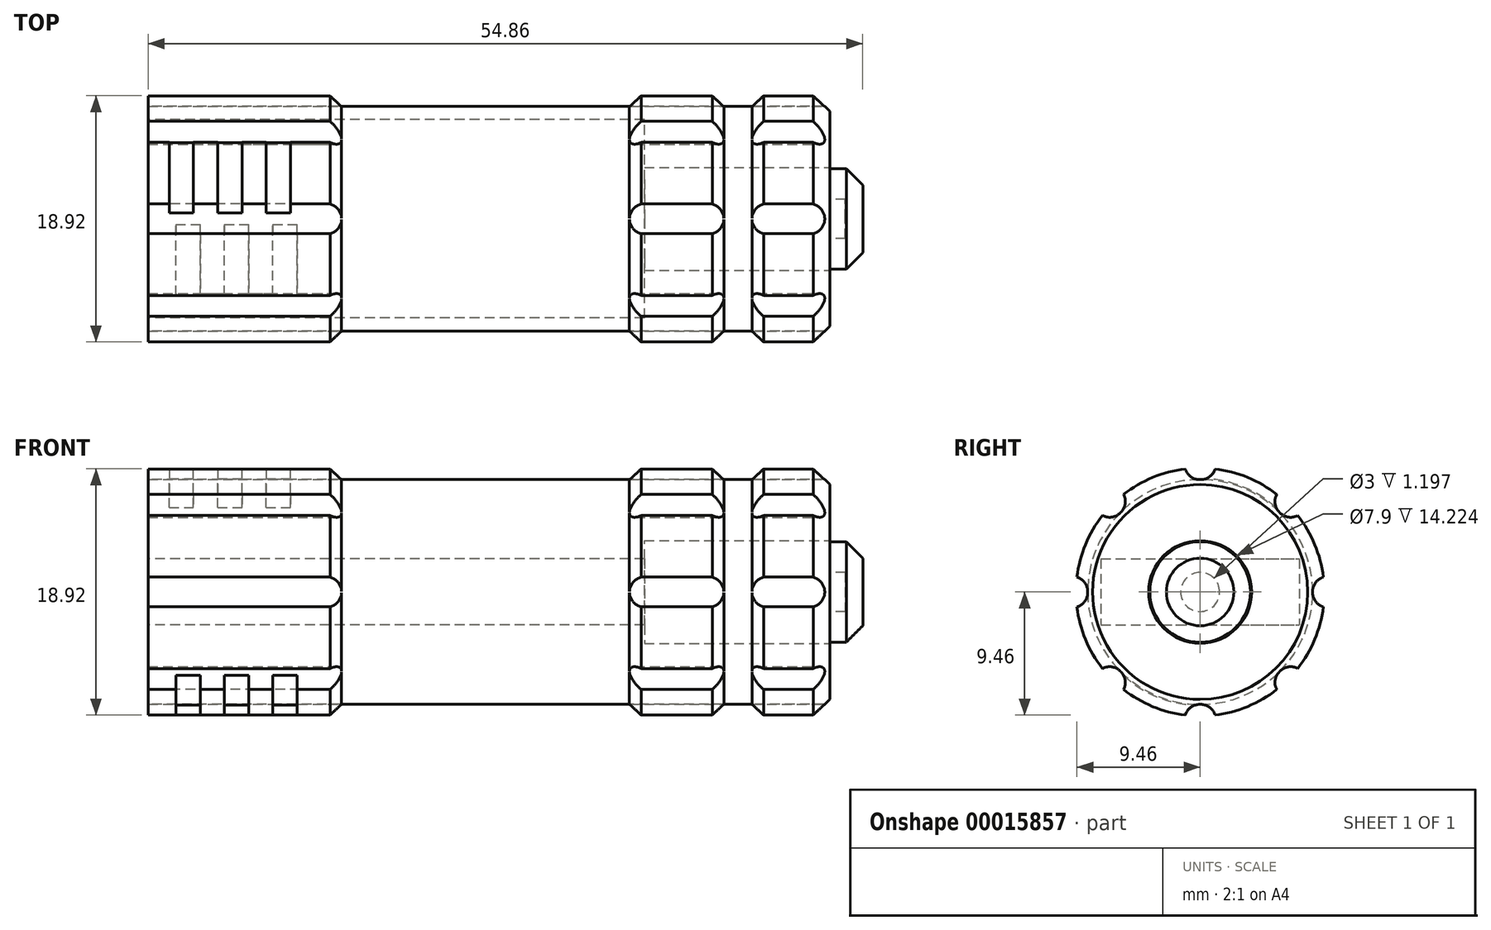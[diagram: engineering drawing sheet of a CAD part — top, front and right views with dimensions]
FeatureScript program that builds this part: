
annotation { "Feature Type Name" : "Feature", "Feature Type Description" : "" }
export const myFeature = defineFeature(function(context is Context, id is Id, definition is map)
    precondition{}
    {
        {
            var Q0;
            Q0=qCreatedBy(makeId("Front.planeOp"),FACE);
            var sketch = newSketch(context, id + "F0", { "sketchPlane" : qUnion([Q0])});
            skLineSegment(sketch, "E0", {"start": v(15.48, 9.52) * mm, "end": v(15.48, 8.64) * mm});
            skLineSegment(sketch, "E1", {"start": v(15.48, 8.64) * mm, "end": v(-2.04, 8.64) * mm});
            skLineSegment(sketch, "E2", {"start": v(-2.04, 8.64) * mm, "end": v(-2.04, 9.52) * mm});
            skLineSegment(sketch, "E3", {"start": v(-2.04, 9.52) * mm, "end": v(-21.1, 9.52) * mm});
            skLineSegment(sketch, "E4", {"start": v(-21.1, 9.52) * mm, "end": v(-21.1, 0) * mm});
            skLineSegment(sketch, "E5", {"start": v(21.83, 9.52) * mm, "end": v(21.83, 8.64) * mm});
            skLineSegment(sketch, "E6", {"start": v(21.83, 8.64) * mm, "end": v(24.88, 8.64) * mm});
            skLineSegment(sketch, "E7", {"start": v(24.88, 8.64) * mm, "end": v(24.88, 9.53) * mm});
            skLineSegment(sketch, "E8", {"start": v(15.48, 9.52) * mm, "end": v(21.83, 9.52) * mm});
            skLineSegment(sketch, "E9", {"start": v(24.88, 9.53) * mm, "end": v(31.23, 9.53) * mm});
            skLineSegment(sketch, "E10", {"start": v(31.23, 9.53) * mm, "end": v(31.23, 3.86) * mm});
            skLineSegment(sketch, "E11", {"start": v(31.23, 3.86) * mm, "end": v(33.77, 3.86) * mm});
            skLineSegment(sketch, "E12", {"start": v(33.77, 3.86) * mm, "end": v(33.77, 0) * mm});
            skLineSegment(sketch, "E13", {"start": v(-21.1, 0) * mm, "end": v(33.77, 0) * mm});
            skLineSegment(sketch, "E14", {"start": v(-2.04, 8.64) * mm, "end": v(-2.04, 0) * mm, "construction": true});
            skSolve(sketch);
        }
        {
            var Q0;
            Q0=qSketchRegion(id+"F0",true);
            var Q1;
            Q1=sQuery(id+"F0.wireOp",EDGE,"E4");
            var Q2;
            Q2=sQuery(id+"F0.wireOp",EDGE,"E3");
            var Q3;
            Q3=sQuery(id+"F0.wireOp",EDGE,"E2");
            var Q4;
            Q4=sQuery(id+"F0.wireOp",EDGE,"E1");
            var Q5;
            Q5=sQuery(id+"F0.wireOp",EDGE,"E0");
            var Q6;
            Q6=sQuery(id+"F0.wireOp",EDGE,"E8");
            var Q7;
            Q7=sQuery(id+"F0.wireOp",EDGE,"E5");
            var Q8;
            Q8=sQuery(id+"F0.wireOp",EDGE,"E6");
            var Q9;
            Q9=sQuery(id+"F0.wireOp",EDGE,"E7");
            var Q10;
            Q10=sQuery(id+"F0.wireOp",EDGE,"E9");
            var Q11;
            Q11=sQuery(id+"F0.wireOp",EDGE,"E10");
            var Q12;
            Q12=sQuery(id+"F0.wireOp",EDGE,"E11");
            var Q13;
            Q13=sQuery(id+"F0.wireOp",EDGE,"E12");
            var Q14;
            Q14=sQuery(id+"F0.wireOp",EDGE,"E13");
            revolve(context, id + "F1", {"entities" : qUnion([Q0]), "surfaceEntities" : qUnion([Q1, Q2, Q3, Q4, Q5, Q6, Q7, Q8, Q9, Q10, Q11, Q12, Q13]), "axis" : qUnion([Q14]), "revolveType" : RevolveType.FULL});
        }
        {
            var Q0;
            Q0=makeQuery(id+"F1.opRevolve","SWEPT_EDGE",EDGE,{"disambiguationData":[OSD([sQuery(id+"F0.wireOp",VERTEX,"E2.end")])]});
            var Q1;
            Q1=makeQuery(id+"F1.opRevolve","SWEPT_EDGE",EDGE,{"disambiguationData":[OSD([sQuery(id+"F0.wireOp",EDGE,"E2"),sQuery(id+"F0.wireOp",EDGE,"E3")])]});
            chamfer(context, id + "F2", {"entities" : qUnion([Q0, Q1]), "width" : 5.08 * mm, "tangentPropagation" : true});
        }
        {
            var Q0;
            Q0=makeQuery(id+"F1.opRevolve","SWEPT_EDGE",EDGE,{"disambiguationData":[OSD([sQuery(id+"F0.wireOp",VERTEX,"E8.start")])]});
            var Q1;
            Q1=makeQuery(id+"F1.opRevolve","SWEPT_EDGE",EDGE,{"disambiguationData":[OSD([sQuery(id+"F0.wireOp",VERTEX,"E5.start")])]});
            var Q2;
            Q2=makeQuery(id+"F1.opRevolve","SWEPT_EDGE",EDGE,{"disambiguationData":[OSD([sQuery(id+"F0.wireOp",VERTEX,"E9.start")])]});
            var Q3;
            Q3=makeQuery(id+"F1.opRevolve","SWEPT_EDGE",EDGE,{"disambiguationData":[OSD([sQuery(id+"F0.wireOp",VERTEX,"E10.start")])]});
            var Q4;
            Q4=makeQuery(id+"F1.opRevolve","SWEPT_EDGE",EDGE,{"disambiguationData":[OSD([sQuery(id+"F0.wireOp",VERTEX,"E12.start")])]});
            var Q5;
            Q5=makeQuery(id+"F1.opRevolve","SWEPT_EDGE",EDGE,{"disambiguationData":[OSD([sQuery(id+"F0.wireOp",EDGE,"E0"),sQuery(id+"F0.wireOp",EDGE,"E8")])]});
            var Q6;
            Q6=makeQuery(id+"F1.opRevolve","SWEPT_EDGE",EDGE,{"disambiguationData":[OSD([sQuery(id+"F0.wireOp",EDGE,"E5"),sQuery(id+"F0.wireOp",EDGE,"E6")])]});
            var Q7;
            Q7=makeQuery(id+"F1.opRevolve","SWEPT_EDGE",EDGE,{"disambiguationData":[OSD([sQuery(id+"F0.wireOp",EDGE,"E7"),sQuery(id+"F0.wireOp",EDGE,"E9")])]});
            var Q8;
            Q8=makeQuery(id+"F1.opRevolve","SWEPT_EDGE",EDGE,{"disambiguationData":[OSD([sQuery(id+"F0.wireOp",EDGE,"E9"),sQuery(id+"F0.wireOp",EDGE,"E10")])]});
            var Q9;
            Q9=makeQuery(id+"F1.opRevolve","SWEPT_EDGE",EDGE,{"disambiguationData":[OSD([sQuery(id+"F0.wireOp",EDGE,"E11"),sQuery(id+"F0.wireOp",EDGE,"E12")])]});
            chamfer(context, id + "F3", {"entities" : qUnion([Q0, Q1, Q2, Q3, Q4, Q5, Q6, Q7, Q8, Q9]), "width" : 1.27 * mm, "tangentPropagation" : true});
        }
        {
            var Q0;
            Q0=makeQuery(id+"F1.opRevolve","SWEPT_FACE",FACE,{"disambiguationData":[OSD([sQuery(id+"F0.wireOp",EDGE,"E4")])]});
            var sketch = newSketch(context, id + "F4", { "sketchPlane" : qUnion([Q0])});
            skLineSegment(sketch, "E15", {"start": v(0, 9.52) * mm, "end": v(0, -9.52) * mm, "construction": true});
            skLineSegment(sketch, "E16", {"start": v(-9.52, 0) * mm, "end": v(9.52, 0) * mm, "construction": true});
            skLineSegment(sketch, "E17", {"start": v(-6.74, -6.74) * mm, "end": v(6.74, 6.74) * mm, "construction": true});
            skLineSegment(sketch, "E18", {"start": v(-6.74, 6.74) * mm, "end": v(6.74, -6.74) * mm, "construction": true});
            skLineSegment(sketch, "E19", {"start": v(-5.88, 7.5) * mm, "end": v(0, 0) * mm});
            skLineSegment(sketch, "E20", {"start": v(0, 0) * mm, "end": v(-7.5, 5.88) * mm});
            skLineSegment(sketch, "E21", {"start": v(-5.88, 7.5) * mm, "end": v(-6.74, 6.74) * mm, "construction": true});
            skLineSegment(sketch, "E22", {"start": v(-7.5, 5.88) * mm, "end": v(-6.74, 6.74) * mm, "construction": true});
            skLineSegment(sketch, "E23", {"start": v(-1.14, 9.46) * mm, "end": v(0, 0) * mm});
            skLineSegment(sketch, "E24", {"start": v(0, 0) * mm, "end": v(1.14, 9.46) * mm});
            skLineSegment(sketch, "E25", {"start": v(1.14, 9.46) * mm, "end": v(0, 9.52) * mm, "construction": true});
            skLineSegment(sketch, "E26", {"start": v(-1.14, 9.46) * mm, "end": v(0, 9.52) * mm, "construction": true});
            skLineSegment(sketch, "E27", {"start": v(0, 0) * mm, "end": v(5.88, 7.5) * mm});
            skLineSegment(sketch, "E28", {"start": v(5.88, 7.5) * mm, "end": v(6.74, 6.74) * mm, "construction": true});
            skLineSegment(sketch, "E29", {"start": v(6.74, 6.74) * mm, "end": v(7.5, 5.88) * mm, "construction": true});
            skLineSegment(sketch, "E30", {"start": v(7.5, 5.88) * mm, "end": v(0, 0) * mm});
            skLineSegment(sketch, "E31", {"start": v(0, 0) * mm, "end": v(9.46, 1.14) * mm});
            skLineSegment(sketch, "E32", {"start": v(9.46, 1.14) * mm, "end": v(9.53, 0) * mm, "construction": true});
            skLineSegment(sketch, "E33", {"start": v(0, 0) * mm, "end": v(9.46, -1.14) * mm});
            skLineSegment(sketch, "E34", {"start": v(9.46, -1.14) * mm, "end": v(9.53, 0) * mm, "construction": true});
            skLineSegment(sketch, "E35", {"start": v(0, 0) * mm, "end": v(7.5, -5.88) * mm});
            skLineSegment(sketch, "E36", {"start": v(7.5, -5.88) * mm, "end": v(6.74, -6.74) * mm, "construction": true});
            skLineSegment(sketch, "E37", {"start": v(0, 0) * mm, "end": v(5.88, -7.5) * mm});
            skLineSegment(sketch, "E38", {"start": v(5.88, -7.5) * mm, "end": v(6.74, -6.74) * mm, "construction": true});
            skLineSegment(sketch, "E39", {"start": v(0, 0) * mm, "end": v(1.14, -9.46) * mm});
            skLineSegment(sketch, "E40", {"start": v(1.14, -9.46) * mm, "end": v(0, -9.52) * mm, "construction": true});
            skLineSegment(sketch, "E41", {"start": v(0, 0) * mm, "end": v(-1.14, -9.46) * mm});
            skLineSegment(sketch, "E42", {"start": v(-1.14, -9.46) * mm, "end": v(0, -9.52) * mm, "construction": true});
            skLineSegment(sketch, "E43", {"start": v(0, 0) * mm, "end": v(-5.88, -7.5) * mm});
            skLineSegment(sketch, "E44", {"start": v(-5.88, -7.5) * mm, "end": v(-6.74, -6.74) * mm, "construction": true});
            skLineSegment(sketch, "E45", {"start": v(0, 0) * mm, "end": v(-7.5, -5.88) * mm});
            skLineSegment(sketch, "E46", {"start": v(-7.5, -5.88) * mm, "end": v(-6.74, -6.74) * mm, "construction": true});
            skLineSegment(sketch, "E47", {"start": v(0, 0) * mm, "end": v(-9.46, -1.14) * mm});
            skLineSegment(sketch, "E48", {"start": v(-9.46, -1.14) * mm, "end": v(-9.52, 0) * mm, "construction": true});
            skLineSegment(sketch, "E49", {"start": v(0, 0) * mm, "end": v(-9.46, 1.14) * mm});
            skLineSegment(sketch, "E50", {"start": v(-9.46, 1.14) * mm, "end": v(-9.52, 0) * mm, "construction": true});
            skLineSegment(sketch, "E51", {"start": v(-5.88, 7.5) * mm, "end": v(-1.14, 9.46) * mm, "construction": true});
            skLineSegment(sketch, "E52", {"start": v(1.14, 9.46) * mm, "end": v(5.88, 7.5) * mm, "construction": true});
            skLineSegment(sketch, "E53", {"start": v(7.5, 5.88) * mm, "end": v(9.46, 1.14) * mm, "construction": true});
            skLineSegment(sketch, "E54", {"start": v(9.46, -1.14) * mm, "end": v(7.5, -5.88) * mm, "construction": true});
            skLineSegment(sketch, "E55", {"start": v(5.88, -7.5) * mm, "end": v(1.14, -9.46) * mm, "construction": true});
            skLineSegment(sketch, "E56", {"start": v(-1.14, -9.46) * mm, "end": v(-5.88, -7.5) * mm, "construction": true});
            skLineSegment(sketch, "E57", {"start": v(-7.5, -5.88) * mm, "end": v(-9.46, -1.14) * mm, "construction": true});
            skLineSegment(sketch, "E58", {"start": v(-9.46, 1.14) * mm, "end": v(-7.5, 5.88) * mm, "construction": true});
            skCircle(sketch, "E59", {"center": v(0, 0) * mm, "radius": 8.64 * mm});
            skLineSegment(sketch, "E60", {"start": v(0, 9.52) * mm, "end": v(0, 8.64) * mm, "construction": true});
            skSolve(sketch);
        }
        {
            var Q0;
            {var subQ3=sQuery(id+"F4.wireOp",EDGE,"E23");var subQ5=sQuery(id+"F4.wireOp",EDGE,"E59");var subQ7=makeQuery(id+"F4.imprint","INTERSECT",VERTEX,{"derivedFrom":[subQ3,subQ5]});Q0=makeQuery(id+"F4.imprint","IMPRINT",FACE,{"disambiguationData":[TD([[makeQuery(id+"F4.imprint","IMPRINT",EDGE,{"disambiguationData":[TD([[subQ7,1.0]])],"derivedFrom":subQ5}),-1.0]])]});}
            var Q1;
            {var subQ3=sQuery(id+"F4.wireOp",EDGE,"E19");var subQ5=sQuery(id+"F4.wireOp",EDGE,"E59");var subQ7=makeQuery(id+"F4.imprint","INTERSECT",VERTEX,{"derivedFrom":[subQ3,subQ5]});Q1=makeQuery(id+"F4.imprint","IMPRINT",FACE,{"disambiguationData":[TD([[makeQuery(id+"F4.imprint","IMPRINT",EDGE,{"disambiguationData":[TD([[subQ7,-1.0]])],"derivedFrom":subQ5}),-1.0]])]});}
            var Q2;
            {var subQ3=sQuery(id+"F4.wireOp",EDGE,"E47");var subQ5=sQuery(id+"F4.wireOp",EDGE,"E59");var subQ7=makeQuery(id+"F4.imprint","INTERSECT",VERTEX,{"derivedFrom":[subQ3,subQ5]});Q2=makeQuery(id+"F4.imprint","IMPRINT",FACE,{"disambiguationData":[TD([[makeQuery(id+"F4.imprint","IMPRINT",EDGE,{"disambiguationData":[TD([[subQ7,1.0]])],"derivedFrom":subQ5}),-1.0]])]});}
            var Q3;
            {var subQ3=sQuery(id+"F4.wireOp",EDGE,"E43");var subQ5=sQuery(id+"F4.wireOp",EDGE,"E59");var subQ7=makeQuery(id+"F4.imprint","INTERSECT",VERTEX,{"derivedFrom":[subQ3,subQ5]});Q3=makeQuery(id+"F4.imprint","IMPRINT",FACE,{"disambiguationData":[TD([[makeQuery(id+"F4.imprint","IMPRINT",EDGE,{"disambiguationData":[TD([[subQ7,1.0]])],"derivedFrom":subQ5}),-1.0]])]});}
            var Q4;
            {var subQ3=sQuery(id+"F4.wireOp",EDGE,"E39");var subQ5=sQuery(id+"F4.wireOp",EDGE,"E59");var subQ7=makeQuery(id+"F4.imprint","INTERSECT",VERTEX,{"derivedFrom":[subQ3,subQ5]});Q4=makeQuery(id+"F4.imprint","IMPRINT",FACE,{"disambiguationData":[TD([[makeQuery(id+"F4.imprint","IMPRINT",EDGE,{"disambiguationData":[TD([[subQ7,1.0]])],"derivedFrom":subQ5}),-1.0]])]});}
            var Q5;
            {var subQ3=sQuery(id+"F4.wireOp",EDGE,"E35");var subQ5=sQuery(id+"F4.wireOp",EDGE,"E59");var subQ7=makeQuery(id+"F4.imprint","INTERSECT",VERTEX,{"derivedFrom":[subQ3,subQ5]});Q5=makeQuery(id+"F4.imprint","IMPRINT",FACE,{"disambiguationData":[TD([[makeQuery(id+"F4.imprint","IMPRINT",EDGE,{"disambiguationData":[TD([[subQ7,1.0]])],"derivedFrom":subQ5}),-1.0]])]});}
            var Q6;
            {var subQ3=sQuery(id+"F4.wireOp",EDGE,"E31");var subQ5=sQuery(id+"F4.wireOp",EDGE,"E59");var subQ7=makeQuery(id+"F4.imprint","INTERSECT",VERTEX,{"derivedFrom":[subQ3,subQ5]});Q6=makeQuery(id+"F4.imprint","IMPRINT",FACE,{"disambiguationData":[TD([[makeQuery(id+"F4.imprint","IMPRINT",EDGE,{"disambiguationData":[TD([[subQ7,1.0]])],"derivedFrom":subQ5}),-1.0]])]});}
            var Q7;
            {var subQ3=sQuery(id+"F4.wireOp",EDGE,"E27");var subQ5=sQuery(id+"F4.wireOp",EDGE,"E59");var subQ7=makeQuery(id+"F4.imprint","INTERSECT",VERTEX,{"derivedFrom":[subQ3,subQ5]});Q7=makeQuery(id+"F4.imprint","IMPRINT",FACE,{"disambiguationData":[TD([[makeQuery(id+"F4.imprint","IMPRINT",EDGE,{"disambiguationData":[TD([[subQ7,1.0]])],"derivedFrom":subQ5}),-1.0]])]});}
            var Q8;
            Q8=makeQuery(id+"F1.opRevolve","SWEPT_FACE",FACE,{"disambiguationData":[OSD([sQuery(id+"F0.wireOp",EDGE,"E10")])]});
            extrude(context, id + "F5", {"entities" : qUnion([Q0, Q1, Q2, Q3, Q4, Q5, Q6, Q7]), "operationType" : NewBodyOperationType.REMOVE, "endBound" : BoundingType.THROUGH_ALL, "oppositeDirection" : true, "endBoundEntityFace" : qUnion([Q8]), "depth" : 25.4 * mm});
        }
        {
            var Q0;
            Q0=qCreatedBy(makeId("Front.planeOp"),FACE);
            var sketch = newSketch(context, id + "F6", { "sketchPlane" : qUnion([Q0])});
            skLineSegment(sketch, "E61", {"start": v(-21.13, 9.56) * mm, "end": v(-19.47, 9.56) * mm, "construction": true});
            skLineSegment(sketch, "E62", {"start": v(-19.47, 9.56) * mm, "end": v(-19.47, 8.72) * mm});
            skLineSegment(sketch, "E63", {"start": v(-19.47, 8.72) * mm, "end": v(-17.6, 8.72) * mm});
            skLineSegment(sketch, "E64", {"start": v(-17.6, 8.72) * mm, "end": v(-17.6, 9.56) * mm});
            skLineSegment(sketch, "E65", {"start": v(-17.6, 9.56) * mm, "end": v(-15.75, 9.56) * mm, "construction": true});
            skLineSegment(sketch, "E66", {"start": v(-15.75, 9.56) * mm, "end": v(-15.75, 8.72) * mm});
            skLineSegment(sketch, "E67", {"start": v(-15.75, 8.72) * mm, "end": v(-13.88, 8.72) * mm});
            skLineSegment(sketch, "E68", {"start": v(-13.88, 8.72) * mm, "end": v(-13.88, 9.56) * mm});
            skLineSegment(sketch, "E69", {"start": v(-13.88, 9.56) * mm, "end": v(-12.03, 9.56) * mm, "construction": true});
            skLineSegment(sketch, "E70", {"start": v(-12.03, 9.56) * mm, "end": v(-12.03, 8.72) * mm});
            skLineSegment(sketch, "E71", {"start": v(-12.03, 8.72) * mm, "end": v(-10.16, 8.72) * mm});
            skLineSegment(sketch, "E72", {"start": v(-10.16, 8.72) * mm, "end": v(-10.16, 9.56) * mm});
            skLineSegment(sketch, "E73", {"start": v(-10.16, 9.56) * mm, "end": v(-7.16, 9.56) * mm, "construction": true});
            skLineSegment(sketch, "E74", {"start": v(-21.13, 0) * mm, "end": v(-7.1, 0) * mm, "construction": true});
            skLineSegment(sketch, "E75", {"start": v(-21.13, 9.56) * mm, "end": v(-21.13, 0) * mm, "construction": true});
            skLineSegment(sketch, "E76", {"start": v(-19.47, 9.56) * mm, "end": v(-17.6, 9.56) * mm});
            skLineSegment(sketch, "E77", {"start": v(-15.75, 9.56) * mm, "end": v(-13.88, 9.56) * mm});
            skLineSegment(sketch, "E78", {"start": v(-12.03, 9.56) * mm, "end": v(-10.16, 9.56) * mm});
            skSolve(sketch);
        }
        {
            var Q0;
            Q0=qSketchRegion(id+"F6",true);
            var Q1;
            Q1=sQuery(id+"F6.wireOp",EDGE,"E74");
            revolve(context, id + "F7", {"operationType" : NewBodyOperationType.REMOVE, "entities" : qUnion([Q0]), "axis" : qUnion([Q1]), "revolveType" : RevolveType.ONE_DIRECTION, "oppositeDirection" : true, "angle" : 41.96 * degree});
        }
        {
            var Q0;
            Q0=qCreatedBy(makeId("Front.planeOp"),FACE);
            var sketch = newSketch(context, id + "F8", { "sketchPlane" : qUnion([Q0])});
            skLineSegment(sketch, "E79", {"start": v(-21.02, -8.7) * mm, "end": v(-18.96, -8.7) * mm, "construction": true});
            skLineSegment(sketch, "E80", {"start": v(-18.96, -8.7) * mm, "end": v(-18.96, -9.55) * mm});
            skLineSegment(sketch, "E81", {"start": v(-18.96, -9.55) * mm, "end": v(-17.08, -9.55) * mm});
            skLineSegment(sketch, "E82", {"start": v(-17.08, -9.55) * mm, "end": v(-17.08, -8.7) * mm});
            skLineSegment(sketch, "E83", {"start": v(-17.08, -8.7) * mm, "end": v(-15.24, -8.7) * mm, "construction": true});
            skLineSegment(sketch, "E84", {"start": v(-15.24, -8.7) * mm, "end": v(-15.24, -9.55) * mm});
            skLineSegment(sketch, "E85", {"start": v(-15.24, -9.55) * mm, "end": v(-13.36, -9.55) * mm});
            skLineSegment(sketch, "E86", {"start": v(-13.36, -9.55) * mm, "end": v(-13.36, -8.7) * mm});
            skLineSegment(sketch, "E87", {"start": v(-13.36, -8.7) * mm, "end": v(-11.52, -8.7) * mm, "construction": true});
            skLineSegment(sketch, "E88", {"start": v(-11.52, -8.7) * mm, "end": v(-11.52, -9.55) * mm});
            skLineSegment(sketch, "E89", {"start": v(-11.52, -9.55) * mm, "end": v(-9.65, -9.55) * mm});
            skLineSegment(sketch, "E90", {"start": v(-9.65, -9.55) * mm, "end": v(-9.65, -8.7) * mm});
            skLineSegment(sketch, "E91", {"start": v(-46.06, -8.7) * mm, "end": v(-9.65, -8.7) * mm, "construction": true});
            skLineSegment(sketch, "E92", {"start": v(-46.06, -0.05) * mm, "end": v(-21.02, -0.05) * mm, "construction": true});
            skLineSegment(sketch, "E93", {"start": v(-21.02, -0.05) * mm, "end": v(-21.02, -8.7) * mm, "construction": true});
            skLineSegment(sketch, "E94", {"start": v(-18.96, -8.7) * mm, "end": v(-17.08, -8.7) * mm});
            skLineSegment(sketch, "E95", {"start": v(-15.24, -8.7) * mm, "end": v(-13.36, -8.7) * mm});
            skLineSegment(sketch, "E96", {"start": v(-11.52, -8.7) * mm, "end": v(-9.65, -8.7) * mm});
            skLineSegment(sketch, "E97", {"start": v(-46.06, -0.05) * mm, "end": v(-46.06, -8.7) * mm, "construction": true});
            skSolve(sketch);
        }
        {
            var Q0;
            Q0=makeQuery(id+"F8.imprint","IMPRINT",FACE,{"disambiguationData":[TD([[makeQuery(id+"F8.imprint","IMPRINT",EDGE,{"derivedFrom":sQuery(id+"F8.wireOp",EDGE,"E88")}),1.0]])]});
            var Q1;
            Q1=makeQuery(id+"F8.imprint","IMPRINT",FACE,{"disambiguationData":[TD([[makeQuery(id+"F8.imprint","IMPRINT",EDGE,{"derivedFrom":sQuery(id+"F8.wireOp",EDGE,"E80")}),1.0]])]});
            var Q2;
            Q2=makeQuery(id+"F8.imprint","IMPRINT",FACE,{"disambiguationData":[TD([[makeQuery(id+"F8.imprint","IMPRINT",EDGE,{"derivedFrom":sQuery(id+"F8.wireOp",EDGE,"E84")}),1.0]])]});
            var Q3;
            Q3=sQuery(id+"F8.wireOp",EDGE,"E95");
            var Q4;
            Q4=sQuery(id+"F8.wireOp",EDGE,"E89");
            var Q5;
            Q5=sQuery(id+"F8.wireOp",EDGE,"E85");
            var Q6;
            Q6=sQuery(id+"F8.wireOp",EDGE,"E81");
            var Q7;
            Q7=sQuery(id+"F8.wireOp",EDGE,"E96");
            var Q8;
            Q8=sQuery(id+"F8.wireOp",EDGE,"E94");
            var Q9;
            Q9=sQuery(id+"F8.wireOp",EDGE,"E90");
            var Q10;
            Q10=sQuery(id+"F8.wireOp",EDGE,"E86");
            var Q11;
            Q11=sQuery(id+"F8.wireOp",EDGE,"E82");
            var Q12;
            Q12=sQuery(id+"F8.wireOp",EDGE,"E88");
            var Q13;
            Q13=sQuery(id+"F8.wireOp",EDGE,"E84");
            var Q14;
            Q14=sQuery(id+"F8.wireOp",EDGE,"E80");
            var Q15;
            Q15=sQuery(id+"F8.wireOp",EDGE,"E92");
            revolve(context, id + "F9", {"operationType" : NewBodyOperationType.REMOVE, "entities" : qUnion([Q0, Q1, Q2]), "surfaceEntities" : qUnion([Q3, Q4, Q5, Q6, Q7, Q8, Q9, Q10, Q11, Q12, Q13, Q14]), "axis" : qUnion([Q15]), "revolveType" : RevolveType.ONE_DIRECTION, "oppositeDirection" : true, "angle" : 41.45 * degree});
        }
        {
            var Q0;
            Q0=makeQuery(id+"F1.opRevolve","SWEPT_FACE",FACE,{"disambiguationData":[OSD([sQuery(id+"F0.wireOp",EDGE,"E4")])]});
            var sketch = newSketch(context, id + "F10", { "sketchPlane" : qUnion([Q0])});
            skLineSegment(sketch, "E98.rect.bottom", {"start": v(7.62, 2.54) * mm, "end": v(-7.62, 2.54) * mm});
            skLineSegment(sketch, "E98.rect.top", {"start": v(7.62, -2.54) * mm, "end": v(-7.62, -2.54) * mm});
            skLineSegment(sketch, "E98.rect.left", {"start": v(7.62, 2.54) * mm, "end": v(7.62, -2.54) * mm});
            skLineSegment(sketch, "E98.rect.right", {"start": v(-7.62, 2.54) * mm, "end": v(-7.62, -2.54) * mm});
            skPoint(sketch, "E98.rect.middle", {"position": v(0, 0) * mm});
            skSolve(sketch);
        }
        {
            var Q0;
            Q0 = qSketchRegion(id + "F10", true);
            extrude(context, id + "F11", {"entities" : qUnion([Q0]), "operationType" : NewBodyOperationType.REMOVE, "oppositeDirection" : true, "depth" : 38.1 * mm});
        }
        {
            var Q0;
            Q0=makeQuery(id+"F1.opRevolve","SWEPT_FACE",FACE,{"disambiguationData":[OSD([sQuery(id+"F0.wireOp",EDGE,"E10")])]});
            var sketch = newSketch(context, id + "F12", { "sketchPlane" : qUnion([Q0])});
            skCircle(sketch, "E99", {"center": v(0, 0) * mm, "radius": 3.95 * mm});
            skSolve(sketch);
        }
        {
            var Q0;
            Q0 = qSketchRegion(id + "F12", true);
            var Q1;
            Q1=makeQuery(id+"F11.boolean.opBoolean","COPY",FACE,{"derivedFrom":makeQuery(id+"F11.opExtrude","CAP_FACE",FACE,{"disambiguationData":[OSD([sQuery(id+"F10.wireOp",EDGE,"E98.rect.bottom"),sQuery(id+"F10.wireOp",EDGE,"E98.rect.top"),sQuery(id+"F10.wireOp",EDGE,"E98.rect.left"),sQuery(id+"F10.wireOp",EDGE,"E98.rect.right")])],"isStart":false})});
            extrude(context, id + "F13", {"entities" : qUnion([Q0]), "operationType" : NewBodyOperationType.REMOVE, "endBound" : BoundingType.UP_TO_SURFACE, "oppositeDirection" : true, "endBoundEntityFace" : qUnion([Q1]), "depth" : 25.4 * mm});
        }
        {
            var Q0;
            Q0=makeQuery(id+"F5.boolean.opBoolean","COPY",EDGE,{"disambiguationData":[OD(0.0)],"derivedFrom":makeQuery(id+"F5.opExtrude","SWEPT_EDGE",EDGE,{"disambiguationData":[OSD([sQuery(id+"F4.wireOp",EDGE,"E47"),sQuery(id+"F4.wireOp",EDGE,"E59")])]})});
            var Q1;
            Q1=makeQuery(id+"F5.boolean.opBoolean","COPY",EDGE,{"disambiguationData":[OD(0.0)],"derivedFrom":makeQuery(id+"F5.opExtrude","SWEPT_EDGE",EDGE,{"disambiguationData":[OSD([sQuery(id+"F4.wireOp",EDGE,"E49"),sQuery(id+"F4.wireOp",EDGE,"E59")])]})});
            var Q2;
            Q2=makeQuery(id+"F5.boolean.opBoolean","COPY",EDGE,{"disambiguationData":[OD(2.0)],"derivedFrom":makeQuery(id+"F5.opExtrude","SWEPT_EDGE",EDGE,{"disambiguationData":[OSD([sQuery(id+"F4.wireOp",EDGE,"E47"),sQuery(id+"F4.wireOp",EDGE,"E59")])]})});
            var Q3;
            Q3=makeQuery(id+"F5.boolean.opBoolean","COPY",EDGE,{"disambiguationData":[OD(1.0)],"derivedFrom":makeQuery(id+"F5.opExtrude","SWEPT_EDGE",EDGE,{"disambiguationData":[OSD([sQuery(id+"F4.wireOp",EDGE,"E47"),sQuery(id+"F4.wireOp",EDGE,"E59")])]})});
            var Q4;
            Q4=makeQuery(id+"F5.boolean.opBoolean","COPY",EDGE,{"disambiguationData":[OD(2.0)],"derivedFrom":makeQuery(id+"F5.opExtrude","SWEPT_EDGE",EDGE,{"disambiguationData":[OSD([sQuery(id+"F4.wireOp",EDGE,"E43"),sQuery(id+"F4.wireOp",EDGE,"E59")])]})});
            var Q5;
            Q5=makeQuery(id+"F5.boolean.opBoolean","COPY",EDGE,{"disambiguationData":[OD(1.0)],"derivedFrom":makeQuery(id+"F5.opExtrude","SWEPT_EDGE",EDGE,{"disambiguationData":[OSD([sQuery(id+"F4.wireOp",EDGE,"E43"),sQuery(id+"F4.wireOp",EDGE,"E59")])]})});
            var Q6;
            Q6=makeQuery(id+"F5.boolean.opBoolean","COPY",EDGE,{"disambiguationData":[OD(0.0)],"derivedFrom":makeQuery(id+"F5.opExtrude","SWEPT_EDGE",EDGE,{"disambiguationData":[OSD([sQuery(id+"F4.wireOp",EDGE,"E43"),sQuery(id+"F4.wireOp",EDGE,"E59")])]})});
            var Q7;
            Q7=makeQuery(id+"F5.boolean.opBoolean","COPY",EDGE,{"disambiguationData":[OD(0.0)],"derivedFrom":makeQuery(id+"F5.opExtrude","SWEPT_EDGE",EDGE,{"disambiguationData":[OSD([sQuery(id+"F4.wireOp",EDGE,"E39"),sQuery(id+"F4.wireOp",EDGE,"E59")])]})});
            var Q8;
            Q8=makeQuery(id+"F5.boolean.opBoolean","COPY",EDGE,{"disambiguationData":[OD(2.0)],"derivedFrom":makeQuery(id+"F5.opExtrude","SWEPT_EDGE",EDGE,{"disambiguationData":[OSD([sQuery(id+"F4.wireOp",EDGE,"E39"),sQuery(id+"F4.wireOp",EDGE,"E59")])]})});
            var Q9;
            Q9=makeQuery(id+"F5.boolean.opBoolean","COPY",EDGE,{"disambiguationData":[OD(1.0)],"derivedFrom":makeQuery(id+"F5.opExtrude","SWEPT_EDGE",EDGE,{"disambiguationData":[OSD([sQuery(id+"F4.wireOp",EDGE,"E39"),sQuery(id+"F4.wireOp",EDGE,"E59")])]})});
            var Q10;
            Q10=makeQuery(id+"F5.boolean.opBoolean","COPY",EDGE,{"disambiguationData":[OD(1.0)],"derivedFrom":makeQuery(id+"F5.opExtrude","SWEPT_EDGE",EDGE,{"disambiguationData":[OSD([sQuery(id+"F4.wireOp",EDGE,"E35"),sQuery(id+"F4.wireOp",EDGE,"E59")])]})});
            var Q11;
            Q11=makeQuery(id+"F5.boolean.opBoolean","COPY",EDGE,{"disambiguationData":[OD(2.0)],"derivedFrom":makeQuery(id+"F5.opExtrude","SWEPT_EDGE",EDGE,{"disambiguationData":[OSD([sQuery(id+"F4.wireOp",EDGE,"E35"),sQuery(id+"F4.wireOp",EDGE,"E59")])]})});
            var Q12;
            Q12=makeQuery(id+"F5.boolean.opBoolean","COPY",EDGE,{"disambiguationData":[OD(0.0)],"derivedFrom":makeQuery(id+"F5.opExtrude","SWEPT_EDGE",EDGE,{"disambiguationData":[OSD([sQuery(id+"F4.wireOp",EDGE,"E35"),sQuery(id+"F4.wireOp",EDGE,"E59")])]})});
            var Q13;
            Q13=makeQuery(id+"F5.boolean.opBoolean","COPY",EDGE,{"disambiguationData":[OD(0.0)],"derivedFrom":makeQuery(id+"F5.opExtrude","SWEPT_EDGE",EDGE,{"disambiguationData":[OSD([sQuery(id+"F4.wireOp",EDGE,"E31"),sQuery(id+"F4.wireOp",EDGE,"E59")])]})});
            var Q14;
            Q14=makeQuery(id+"F5.boolean.opBoolean","COPY",EDGE,{"disambiguationData":[OD(2.0)],"derivedFrom":makeQuery(id+"F5.opExtrude","SWEPT_EDGE",EDGE,{"disambiguationData":[OSD([sQuery(id+"F4.wireOp",EDGE,"E31"),sQuery(id+"F4.wireOp",EDGE,"E59")])]})});
            var Q15;
            Q15=makeQuery(id+"F5.boolean.opBoolean","COPY",EDGE,{"disambiguationData":[OD(1.0)],"derivedFrom":makeQuery(id+"F5.opExtrude","SWEPT_EDGE",EDGE,{"disambiguationData":[OSD([sQuery(id+"F4.wireOp",EDGE,"E31"),sQuery(id+"F4.wireOp",EDGE,"E59")])]})});
            var Q16;
            Q16=makeQuery(id+"F5.boolean.opBoolean","COPY",EDGE,{"disambiguationData":[OD(0.0)],"derivedFrom":makeQuery(id+"F5.opExtrude","SWEPT_EDGE",EDGE,{"disambiguationData":[OSD([sQuery(id+"F4.wireOp",EDGE,"E27"),sQuery(id+"F4.wireOp",EDGE,"E59")])]})});
            var Q17;
            Q17=makeQuery(id+"F5.boolean.opBoolean","COPY",EDGE,{"disambiguationData":[OD(2.0)],"derivedFrom":makeQuery(id+"F5.opExtrude","SWEPT_EDGE",EDGE,{"disambiguationData":[OSD([sQuery(id+"F4.wireOp",EDGE,"E27"),sQuery(id+"F4.wireOp",EDGE,"E59")])]})});
            var Q18;
            Q18=makeQuery(id+"F5.boolean.opBoolean","COPY",EDGE,{"disambiguationData":[OD(1.0)],"derivedFrom":makeQuery(id+"F5.opExtrude","SWEPT_EDGE",EDGE,{"disambiguationData":[OSD([sQuery(id+"F4.wireOp",EDGE,"E27"),sQuery(id+"F4.wireOp",EDGE,"E59")])]})});
            var Q19;
            Q19=makeQuery(id+"F5.boolean.opBoolean","COPY",EDGE,{"disambiguationData":[OD(0.0)],"derivedFrom":makeQuery(id+"F5.opExtrude","SWEPT_EDGE",EDGE,{"disambiguationData":[OSD([sQuery(id+"F4.wireOp",EDGE,"E23"),sQuery(id+"F4.wireOp",EDGE,"E59")])]})});
            var Q20;
            Q20=makeQuery(id+"F5.boolean.opBoolean","COPY",EDGE,{"disambiguationData":[OD(2.0)],"derivedFrom":makeQuery(id+"F5.opExtrude","SWEPT_EDGE",EDGE,{"disambiguationData":[OSD([sQuery(id+"F4.wireOp",EDGE,"E23"),sQuery(id+"F4.wireOp",EDGE,"E59")])]})});
            var Q21;
            Q21=makeQuery(id+"F5.boolean.opBoolean","COPY",EDGE,{"disambiguationData":[OD(1.0)],"derivedFrom":makeQuery(id+"F5.opExtrude","SWEPT_EDGE",EDGE,{"disambiguationData":[OSD([sQuery(id+"F4.wireOp",EDGE,"E23"),sQuery(id+"F4.wireOp",EDGE,"E59")])]})});
            var Q22;
            Q22=makeQuery(id+"F5.boolean.opBoolean","COPY",EDGE,{"disambiguationData":[OD(0.0)],"derivedFrom":makeQuery(id+"F5.opExtrude","SWEPT_EDGE",EDGE,{"disambiguationData":[OSD([sQuery(id+"F4.wireOp",EDGE,"E20"),sQuery(id+"F4.wireOp",EDGE,"E59")])]})});
            var Q23;
            Q23=makeQuery(id+"F5.boolean.opBoolean","COPY",EDGE,{"disambiguationData":[OD(2.0)],"derivedFrom":makeQuery(id+"F5.opExtrude","SWEPT_EDGE",EDGE,{"disambiguationData":[OSD([sQuery(id+"F4.wireOp",EDGE,"E20"),sQuery(id+"F4.wireOp",EDGE,"E59")])]})});
            var Q24;
            Q24=makeQuery(id+"F5.boolean.opBoolean","COPY",EDGE,{"disambiguationData":[OD(1.0)],"derivedFrom":makeQuery(id+"F5.opExtrude","SWEPT_EDGE",EDGE,{"disambiguationData":[OSD([sQuery(id+"F4.wireOp",EDGE,"E20"),sQuery(id+"F4.wireOp",EDGE,"E59")])]})});
            var Q25;
            Q25=makeQuery(id+"F5.boolean.opBoolean","COPY",EDGE,{"disambiguationData":[OD(1.0)],"derivedFrom":makeQuery(id+"F5.opExtrude","SWEPT_EDGE",EDGE,{"disambiguationData":[OSD([sQuery(id+"F4.wireOp",EDGE,"E41"),sQuery(id+"F4.wireOp",EDGE,"E59")])]})});
            var Q26;
            Q26=makeQuery(id+"F5.boolean.opBoolean","COPY",EDGE,{"disambiguationData":[OD(2.0)],"derivedFrom":makeQuery(id+"F5.opExtrude","SWEPT_EDGE",EDGE,{"disambiguationData":[OSD([sQuery(id+"F4.wireOp",EDGE,"E41"),sQuery(id+"F4.wireOp",EDGE,"E59")])]})});
            var Q27;
            Q27=makeQuery(id+"F5.boolean.opBoolean","COPY",EDGE,{"disambiguationData":[OD(0.0)],"derivedFrom":makeQuery(id+"F5.opExtrude","SWEPT_EDGE",EDGE,{"disambiguationData":[OSD([sQuery(id+"F4.wireOp",EDGE,"E41"),sQuery(id+"F4.wireOp",EDGE,"E59")])]})});
            var Q28;
            Q28=makeQuery(id+"F5.boolean.opBoolean","COPY",EDGE,{"disambiguationData":[OD(1.0)],"derivedFrom":makeQuery(id+"F5.opExtrude","SWEPT_EDGE",EDGE,{"disambiguationData":[OSD([sQuery(id+"F4.wireOp",EDGE,"E45"),sQuery(id+"F4.wireOp",EDGE,"E59")])]})});
            var Q29;
            Q29=makeQuery(id+"F5.boolean.opBoolean","COPY",EDGE,{"disambiguationData":[OD(2.0)],"derivedFrom":makeQuery(id+"F5.opExtrude","SWEPT_EDGE",EDGE,{"disambiguationData":[OSD([sQuery(id+"F4.wireOp",EDGE,"E45"),sQuery(id+"F4.wireOp",EDGE,"E59")])]})});
            var Q30;
            Q30=makeQuery(id+"F5.boolean.opBoolean","COPY",EDGE,{"disambiguationData":[OD(0.0)],"derivedFrom":makeQuery(id+"F5.opExtrude","SWEPT_EDGE",EDGE,{"disambiguationData":[OSD([sQuery(id+"F4.wireOp",EDGE,"E45"),sQuery(id+"F4.wireOp",EDGE,"E59")])]})});
            var Q31;
            Q31=makeQuery(id+"F5.boolean.opBoolean","COPY",EDGE,{"disambiguationData":[OD(1.0)],"derivedFrom":makeQuery(id+"F5.opExtrude","SWEPT_EDGE",EDGE,{"disambiguationData":[OSD([sQuery(id+"F4.wireOp",EDGE,"E49"),sQuery(id+"F4.wireOp",EDGE,"E59")])]})});
            var Q32;
            Q32=makeQuery(id+"F5.boolean.opBoolean","COPY",EDGE,{"disambiguationData":[OD(2.0)],"derivedFrom":makeQuery(id+"F5.opExtrude","SWEPT_EDGE",EDGE,{"disambiguationData":[OSD([sQuery(id+"F4.wireOp",EDGE,"E49"),sQuery(id+"F4.wireOp",EDGE,"E59")])]})});
            var Q33;
            Q33=makeQuery(id+"F5.boolean.opBoolean","COPY",EDGE,{"disambiguationData":[OD(1.0)],"derivedFrom":makeQuery(id+"F5.opExtrude","SWEPT_EDGE",EDGE,{"disambiguationData":[OSD([sQuery(id+"F4.wireOp",EDGE,"E19"),sQuery(id+"F4.wireOp",EDGE,"E59")])]})});
            var Q34;
            Q34=makeQuery(id+"F5.boolean.opBoolean","COPY",EDGE,{"disambiguationData":[OD(2.0)],"derivedFrom":makeQuery(id+"F5.opExtrude","SWEPT_EDGE",EDGE,{"disambiguationData":[OSD([sQuery(id+"F4.wireOp",EDGE,"E19"),sQuery(id+"F4.wireOp",EDGE,"E59")])]})});
            var Q35;
            Q35=makeQuery(id+"F5.boolean.opBoolean","COPY",EDGE,{"disambiguationData":[OD(0.0)],"derivedFrom":makeQuery(id+"F5.opExtrude","SWEPT_EDGE",EDGE,{"disambiguationData":[OSD([sQuery(id+"F4.wireOp",EDGE,"E19"),sQuery(id+"F4.wireOp",EDGE,"E59")])]})});
            var Q36;
            Q36=makeQuery(id+"F5.boolean.opBoolean","COPY",EDGE,{"disambiguationData":[OD(1.0)],"derivedFrom":makeQuery(id+"F5.opExtrude","SWEPT_EDGE",EDGE,{"disambiguationData":[OSD([sQuery(id+"F4.wireOp",EDGE,"E24"),sQuery(id+"F4.wireOp",EDGE,"E59")])]})});
            var Q37;
            Q37=makeQuery(id+"F5.boolean.opBoolean","COPY",EDGE,{"disambiguationData":[OD(2.0)],"derivedFrom":makeQuery(id+"F5.opExtrude","SWEPT_EDGE",EDGE,{"disambiguationData":[OSD([sQuery(id+"F4.wireOp",EDGE,"E24"),sQuery(id+"F4.wireOp",EDGE,"E59")])]})});
            var Q38;
            Q38=makeQuery(id+"F5.boolean.opBoolean","COPY",EDGE,{"disambiguationData":[OD(0.0)],"derivedFrom":makeQuery(id+"F5.opExtrude","SWEPT_EDGE",EDGE,{"disambiguationData":[OSD([sQuery(id+"F4.wireOp",EDGE,"E24"),sQuery(id+"F4.wireOp",EDGE,"E59")])]})});
            var Q39;
            Q39=makeQuery(id+"F5.boolean.opBoolean","COPY",EDGE,{"disambiguationData":[OD(1.0)],"derivedFrom":makeQuery(id+"F5.opExtrude","SWEPT_EDGE",EDGE,{"disambiguationData":[OSD([sQuery(id+"F4.wireOp",EDGE,"E30"),sQuery(id+"F4.wireOp",EDGE,"E59")])]})});
            var Q40;
            Q40=makeQuery(id+"F5.boolean.opBoolean","COPY",EDGE,{"disambiguationData":[OD(2.0)],"derivedFrom":makeQuery(id+"F5.opExtrude","SWEPT_EDGE",EDGE,{"disambiguationData":[OSD([sQuery(id+"F4.wireOp",EDGE,"E30"),sQuery(id+"F4.wireOp",EDGE,"E59")])]})});
            var Q41;
            Q41=makeQuery(id+"F5.boolean.opBoolean","COPY",EDGE,{"disambiguationData":[OD(0.0)],"derivedFrom":makeQuery(id+"F5.opExtrude","SWEPT_EDGE",EDGE,{"disambiguationData":[OSD([sQuery(id+"F4.wireOp",EDGE,"E30"),sQuery(id+"F4.wireOp",EDGE,"E59")])]})});
            var Q42;
            Q42=makeQuery(id+"F5.boolean.opBoolean","COPY",EDGE,{"disambiguationData":[OD(1.0)],"derivedFrom":makeQuery(id+"F5.opExtrude","SWEPT_EDGE",EDGE,{"disambiguationData":[OSD([sQuery(id+"F4.wireOp",EDGE,"E33"),sQuery(id+"F4.wireOp",EDGE,"E59")])]})});
            var Q43;
            Q43=makeQuery(id+"F5.boolean.opBoolean","COPY",EDGE,{"disambiguationData":[OD(2.0)],"derivedFrom":makeQuery(id+"F5.opExtrude","SWEPT_EDGE",EDGE,{"disambiguationData":[OSD([sQuery(id+"F4.wireOp",EDGE,"E33"),sQuery(id+"F4.wireOp",EDGE,"E59")])]})});
            var Q44;
            Q44=makeQuery(id+"F5.boolean.opBoolean","COPY",EDGE,{"disambiguationData":[OD(0.0)],"derivedFrom":makeQuery(id+"F5.opExtrude","SWEPT_EDGE",EDGE,{"disambiguationData":[OSD([sQuery(id+"F4.wireOp",EDGE,"E33"),sQuery(id+"F4.wireOp",EDGE,"E59")])]})});
            var Q45;
            Q45=makeQuery(id+"F5.boolean.opBoolean","COPY",EDGE,{"disambiguationData":[OD(1.0)],"derivedFrom":makeQuery(id+"F5.opExtrude","SWEPT_EDGE",EDGE,{"disambiguationData":[OSD([sQuery(id+"F4.wireOp",EDGE,"E37"),sQuery(id+"F4.wireOp",EDGE,"E59")])]})});
            var Q46;
            Q46=makeQuery(id+"F5.boolean.opBoolean","COPY",EDGE,{"disambiguationData":[OD(2.0)],"derivedFrom":makeQuery(id+"F5.opExtrude","SWEPT_EDGE",EDGE,{"disambiguationData":[OSD([sQuery(id+"F4.wireOp",EDGE,"E37"),sQuery(id+"F4.wireOp",EDGE,"E59")])]})});
            var Q47;
            Q47=makeQuery(id+"F5.boolean.opBoolean","COPY",EDGE,{"disambiguationData":[OD(0.0)],"derivedFrom":makeQuery(id+"F5.opExtrude","SWEPT_EDGE",EDGE,{"disambiguationData":[OSD([sQuery(id+"F4.wireOp",EDGE,"E37"),sQuery(id+"F4.wireOp",EDGE,"E59")])]})});
            fillet(context, id + "F14", {"entities" : qUnion([Q0, Q1, Q2, Q3, Q4, Q5, Q6, Q7, Q8, Q9, Q10, Q11, Q12, Q13, Q14, Q15, Q16, Q17, Q18, Q19, Q20, Q21, Q22, Q23, Q24, Q25, Q26, Q27, Q28, Q29, Q30, Q31, Q32, Q33, Q34, Q35, Q36, Q37, Q38, Q39, Q40, Q41, Q42, Q43, Q44, Q45, Q46, Q47]), "radius" : 1.15 * mm, "tangentPropagation" : true, "allowEdgeOverflow" : false});
        }
        {
            var Q0;
            Q0=makeQuery(id+"F13.boolean.opBoolean","COPY",FACE,{"derivedFrom":makeQuery(id+"F13.opExtrude","CAP_FACE",FACE,{"disambiguationData":[OSD([sQuery(id+"F12.wireOp",EDGE,"E99")])],"isStart":true})});
            var sketch = newSketch(context, id + "F15", { "sketchPlane" : qUnion([Q0])});
            skCircle(sketch, "E100", {"center": v(0, 0) * mm, "radius": 1.5 * mm});
            skSolve(sketch);
        }
        {
            var Q0;
            Q0 = qSketchRegion(id + "F15", true);
            extrude(context, id + "F16", {"entities" : qUnion([Q0]), "operationType" : NewBodyOperationType.REMOVE, "oppositeDirection" : true, "depth" : 1.2 * mm});
        }
    });
